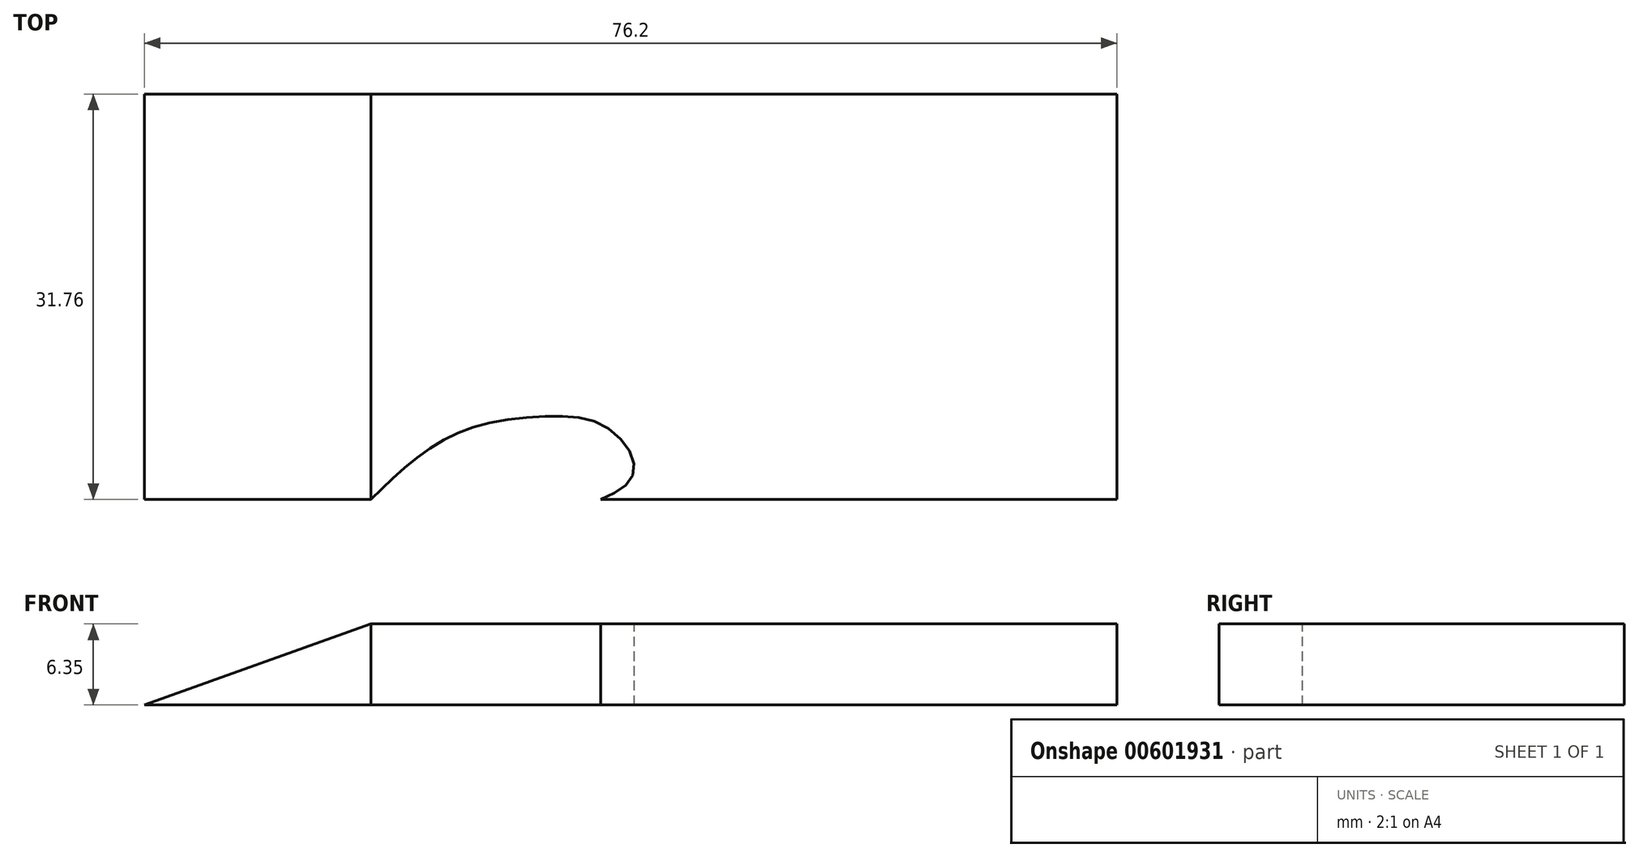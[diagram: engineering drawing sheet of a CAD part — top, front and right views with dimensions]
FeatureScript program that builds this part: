
annotation { "Feature Type Name" : "Feature", "Feature Type Description" : "" }
export const myFeature = defineFeature(function(context is Context, id is Id, definition is map)
    precondition{}
    {
        {
            var Q0;
            Q0=qCreatedBy(makeId("Top.planeOp"),FACE);
            var sketch = newSketch(context, id + "F0", { "sketchPlane" : qUnion([Q0])});
            skLineSegment(sketch, "E0.bottom", {"start": v(-38.1, 15.87) * mm, "end": v(38.1, 15.88) * mm});
            skLineSegment(sketch, "E0.top", {"start": v(-38.1, -15.88) * mm, "end": v(38.1, -15.87) * mm});
            skLineSegment(sketch, "E0.left", {"start": v(-38.1, 15.87) * mm, "end": v(-38.1, -15.88) * mm});
            skLineSegment(sketch, "E0.right", {"start": v(38.1, 15.88) * mm, "end": v(38.1, -15.87) * mm});
            skPoint(sketch, "E0.middle", {"position": v(0, 0) * mm});
            skFitSpline(sketch, "E1", {"points": [v(-20.35, -15.88) * mm, v(-17.84, -13.51) * mm, v(-14.8, -11.3) * mm, v(-11.2, -9.92) * mm, v(-6.23, -9.36) * mm, v(-2.5, -9.92) * mm, v(0, -12.27) * mm, v(0, -14.34) * mm, v(-2.35, -15.88) * mm], "startDerivative": vector(19.44, 19.14) * mm, "endDerivative": vector(-25.67, -11.47) * mm});
            skSolve(sketch);
        }
        {
            var Q0;
            Q0=makeQuery(id+"F0.imprint","IMPRINT",FACE,{"disambiguationData":[TD([[makeQuery(id+"F0.imprint","IMPRINT",EDGE,{"derivedFrom":sQuery(id+"F0.wireOp",EDGE,"E0.bottom")}),-1.0]])]});
            extrude(context, id + "F1", {"entities" : qUnion([Q0]), "depth" : 6.35 * mm, "offsetDistance" : 25.4 * mm});
        }
        {
            var Q0;
            Q0=makeQuery(id+"F1.opExtrude","CAP_EDGE",EDGE,{"disambiguationData":[OSD([sQuery(id+"F0.wireOp",EDGE,"E0.left")])],"isStart":false});
            chamfer(context, id + "F2", {"entities" : qUnion([Q0]), "chamferType" : ChamferType.TWO_OFFSETS, "width1" : 17.75 * mm, "oppositeDirection" : false, "width2" : 6.35 * mm, "tangentPropagation" : true});
        }
    });
